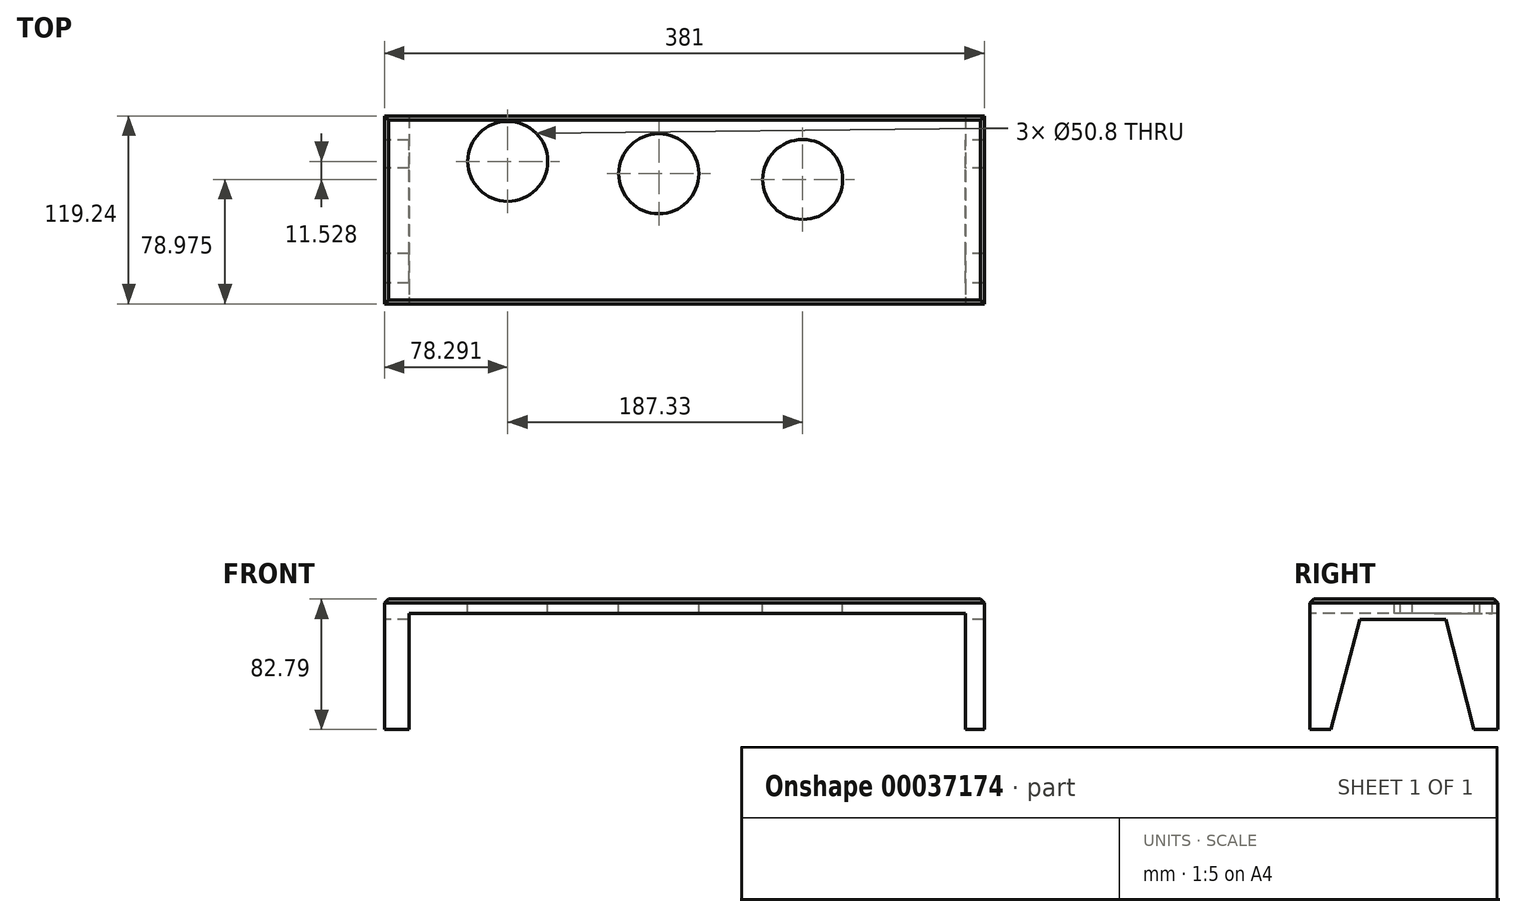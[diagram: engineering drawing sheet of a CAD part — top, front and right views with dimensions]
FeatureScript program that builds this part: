
annotation { "Feature Type Name" : "Feature", "Feature Type Description" : "" }
export const myFeature = defineFeature(function(context is Context, id is Id, definition is map)
    precondition{}
    {
        {
            var Q0;
            Q0=qCreatedBy(makeId("Right.planeOp"),FACE);
            var sketch = newSketch(context, id + "F0", { "sketchPlane" : qUnion([Q0])});
            skLineSegment(sketch, "E0", {"start": v(40.78, -73.52) * mm, "end": v(55.91, -73.52) * mm});
            skLineSegment(sketch, "E1", {"start": v(55.91, -73.52) * mm, "end": v(55.91, 9.27) * mm});
            skLineSegment(sketch, "E2", {"start": v(55.91, 9.27) * mm, "end": v(-63.33, 9.27) * mm});
            skLineSegment(sketch, "E3", {"start": v(-63.33, 9.27) * mm, "end": v(-63.33, -73.52) * mm});
            skLineSegment(sketch, "E4", {"start": v(-63.33, -73.52) * mm, "end": v(-50.04, -73.52) * mm});
            skLineSegment(sketch, "E5", {"start": v(-50.04, -73.52) * mm, "end": v(-31.5, -3.7) * mm});
            skLineSegment(sketch, "E6", {"start": v(-31.5, -3.7) * mm, "end": v(22.86, -3.7) * mm});
            skLineSegment(sketch, "E7", {"start": v(22.86, -3.7) * mm, "end": v(40.78, -73.52) * mm});
            skSolve(sketch);
        }
        {
            var Q0;
            Q0=makeQuery(id+"F0.imprint","IMPRINT",FACE,{"disambiguationData":[TD([[makeQuery(id+"F0.imprint","IMPRINT",EDGE,{"derivedFrom":sQuery(id+"F0.wireOp",EDGE,"E0")}),1.0]])]});
            extrude(context, id + "F1", {"entities" : qUnion([Q0]), "depth" : 381 * mm});
        }
        {
            var Q0;
            Q0=makeQuery(id+"F1.opExtrude","SWEPT_FACE",FACE,{"disambiguationData":[OSD([sQuery(id+"F0.wireOp",EDGE,"E3")])]});
            var sketch = newSketch(context, id + "F2", { "sketchPlane" : qUnion([Q0])});
            skLineSegment(sketch, "E8.bottom", {"start": v(15.71, -73.52) * mm, "end": v(368.96, -73.52) * mm});
            skLineSegment(sketch, "E8.top", {"start": v(15.71, 0) * mm, "end": v(368.96, 0) * mm});
            skLineSegment(sketch, "E8.left", {"start": v(15.71, -73.52) * mm, "end": v(15.71, 0) * mm});
            skLineSegment(sketch, "E8.right", {"start": v(368.96, -73.52) * mm, "end": v(368.96, 0) * mm});
            skSolve(sketch);
        }
        {
            var Q0;
            Q0=makeQuery(id+"F2.imprint","IMPRINT",FACE,{"disambiguationData":[TD([[makeQuery(id+"F2.imprint","IMPRINT",EDGE,{"derivedFrom":sQuery(id+"F2.wireOp",EDGE,"E8.bottom")}),-1.0]])]});
            extrude(context, id + "F3", {"entities" : qUnion([Q0]), "operationType" : NewBodyOperationType.REMOVE, "endBound" : BoundingType.THROUGH_ALL, "oppositeDirection" : true, "depth" : 25.4 * mm});
        }
        {
            var Q0;
            Q0=makeQuery(id+"F1.opExtrude","CAP_EDGE",EDGE,{"disambiguationData":[OSD([sQuery(id+"F0.wireOp",EDGE,"E2")])],"isStart":false});
            var Q1;
            Q1=makeQuery(id+"F1.opExtrude","SWEPT_EDGE",EDGE,{"disambiguationData":[OSD([sQuery(id+"F0.wireOp",EDGE,"E2"),sQuery(id+"F0.wireOp",EDGE,"E3")])]});
            var Q2;
            Q2=makeQuery(id+"F1.opExtrude","SWEPT_EDGE",EDGE,{"disambiguationData":[OSD([sQuery(id+"F0.wireOp",EDGE,"E1"),sQuery(id+"F0.wireOp",EDGE,"E2")])]});
            var Q3;
            Q3=makeQuery(id+"F1.opExtrude","CAP_EDGE",EDGE,{"disambiguationData":[OSD([sQuery(id+"F0.wireOp",EDGE,"E2")])],"isStart":true});
            chamfer(context, id + "F4", {"entities" : qUnion([Q0, Q1, Q2, Q3]), "width" : 2.54 * mm, "tangentPropagation" : true});
        }
        {
            var Q0;
            Q0=makeQuery(id+"F1.opExtrude","SWEPT_FACE",FACE,{"disambiguationData":[OSD([sQuery(id+"F0.wireOp",EDGE,"E2")])]});
            var sketch = newSketch(context, id + "F5", { "sketchPlane" : qUnion([Q0])});
            skCircle(sketch, "E9", {"center": v(78.3, 27.17) * mm, "radius": 19.95 * mm});
            skCircle(sketch, "E10", {"center": v(174.22, 19.35) * mm, "radius": 18.44 * mm});
            skCircle(sketch, "E11", {"center": v(265.62, 15.65) * mm, "radius": 17.97 * mm});
            skSolve(sketch);
        }
        {
            var Q0;
            Q0=sQuery(id+"F5.wireOp",VERTEX,"E9.center");
            var Q1;
            Q1=sQuery(id+"F5.wireOp",VERTEX,"E10.center");
            var Q2;
            Q2=sQuery(id+"F5.wireOp",VERTEX,"E11.center");
            var Q3;
            Q3=makeQuery(id+"F1.opExtrude","SWEPT_BODY",BODY,{"disambiguationData":[OSD([sQuery(id+"F0.wireOp",EDGE,"E0"),sQuery(id+"F0.wireOp",EDGE,"E1"),sQuery(id+"F0.wireOp",EDGE,"E2"),sQuery(id+"F0.wireOp",EDGE,"E3"),sQuery(id+"F0.wireOp",EDGE,"E4"),sQuery(id+"F0.wireOp",EDGE,"E5"),sQuery(id+"F0.wireOp",EDGE,"E6"),sQuery(id+"F0.wireOp",EDGE,"E7")])]});
            hole(context, id + "F6", {"style" : HoleStyle.SIMPLE, "holeDiameter" : 50.8 * mm, "endStyle" : HoleEndStyle.THROUGH, "locations" : qUnion([Q0, Q1, Q2]), "scope" : qUnion([Q3])});
        }
    });
